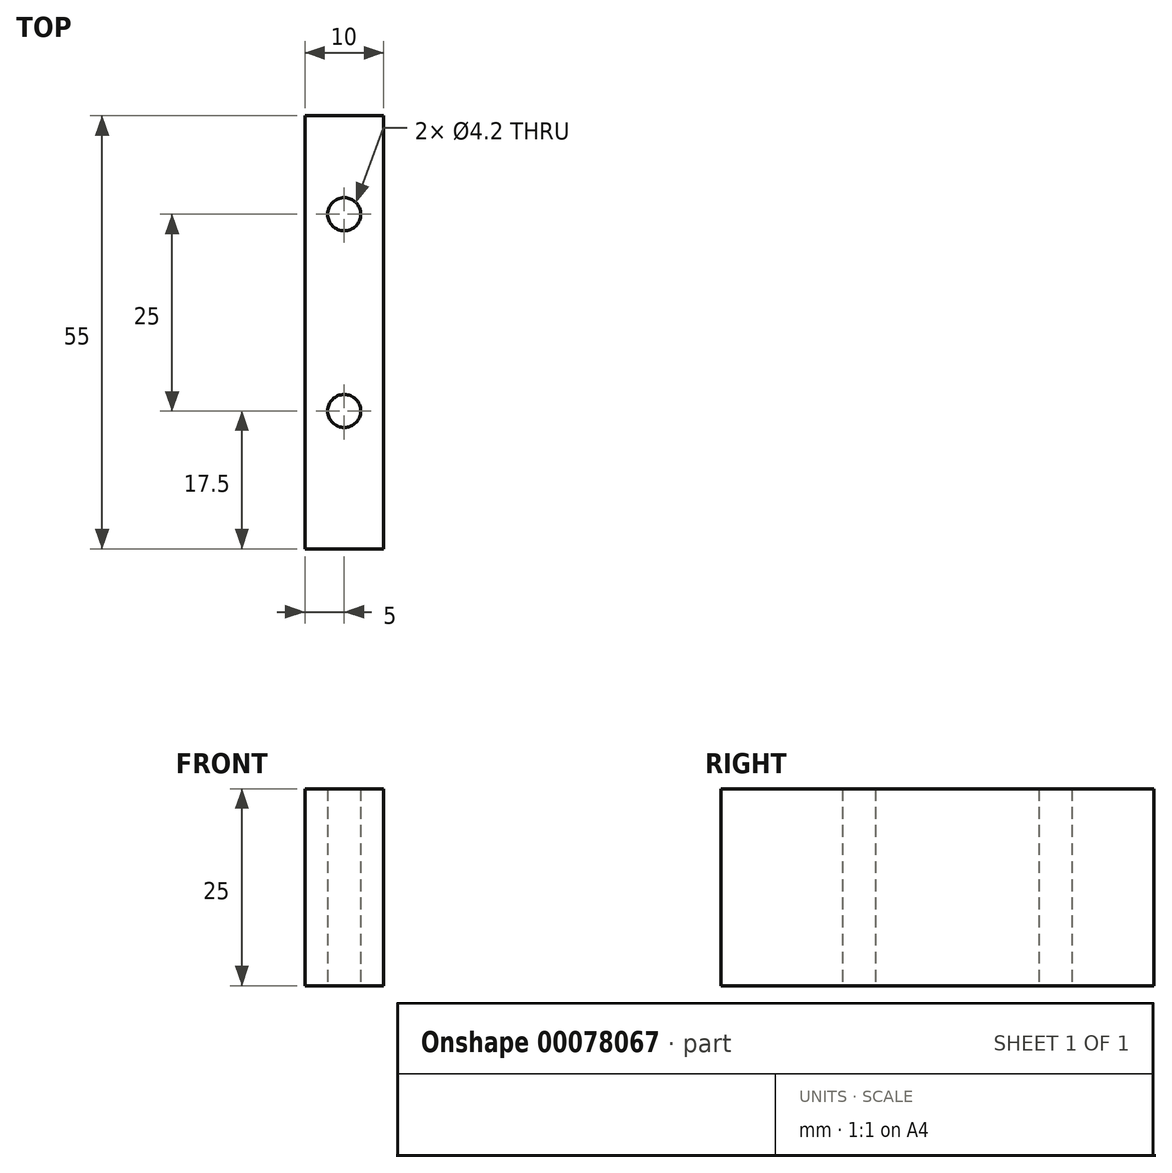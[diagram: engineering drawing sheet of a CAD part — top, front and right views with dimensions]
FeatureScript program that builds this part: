
annotation { "Feature Type Name" : "Feature", "Feature Type Description" : "" }
export const myFeature = defineFeature(function(context is Context, id is Id, definition is map)
    precondition{}
    {
        {
            var Q0;
            Q0=qCreatedBy(makeId("Top.planeOp"),FACE);
            var sketch = newSketch(context, id + "F0", { "sketchPlane" : qUnion([Q0])});
            skLineSegment(sketch, "E0.bottom", {"start": v(5, 27.5) * mm, "end": v(-5, 27.5) * mm});
            skLineSegment(sketch, "E0.top", {"start": v(5, -27.5) * mm, "end": v(-5, -27.5) * mm});
            skLineSegment(sketch, "E0.left", {"start": v(5, 27.5) * mm, "end": v(5, -27.5) * mm});
            skLineSegment(sketch, "E0.right", {"start": v(-5, 27.5) * mm, "end": v(-5, -27.5) * mm});
            skPoint(sketch, "E0.middle", {"position": v(0, 0) * mm});
            skCircle(sketch, "E1", {"center": v(0, 15) * mm, "radius": 2.1 * mm});
            skCircle(sketch, "E2", {"center": v(0, -10) * mm, "radius": 2.1 * mm});
            skSolve(sketch);
        }
        {
            var Q0;
            Q0=makeQuery(id+"F0.imprint","IMPRINT",FACE,{"disambiguationData":[TD([[makeQuery(id+"F0.imprint","IMPRINT",EDGE,{"derivedFrom":sQuery(id+"F0.wireOp",EDGE,"E0.bottom")}),1.0]])]});
            extrude(context, id + "F1", {"entities" : qUnion([Q0]), "depth" : 25 * mm, "offsetDistance" : 25 * mm});
        }
    });
